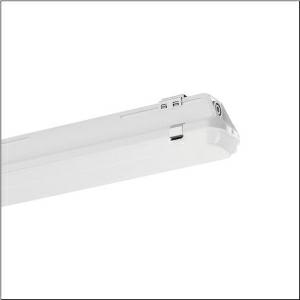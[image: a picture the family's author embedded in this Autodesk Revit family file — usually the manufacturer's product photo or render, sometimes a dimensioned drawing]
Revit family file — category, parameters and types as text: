
# Revit family: monsun_r__21_emergency_51fb20dp467c3h_1d79
name_source: partatom
category: Lighting Fixtures
units: mm (PartAtom-declared; Revit-internal decimal feet)

## family parameters
Cut with Voids When Loaded = No
Host = Face
Light Source = No
Part Type = Normal
Room Calculation Point = No
Round Connector Dimension = Use Diameter
Shared = No

## types (1)
- --- (1 x LED, 5460 lm, 36.5 W, 4000K)
    Apparent Load = 37 VA
    CIE Flux Codes = 45 75 93 94 100
    Color Rendering = 80
    Color Temperature = 4000K
    Default Elevation = 1800 mm
    Description = Monsun® 21 emergency, damp-proof luminaire, chain hanger, primary optical cover: enclosure, of PC, light emission: direct distribution, primary light characteristic: symmetric, installation type: vertical mounting, horizontal mounting, surface-mounted, suspended mounting, LED, rated luminous flux: 5.460lm, luminous efficacy: 167lm/W, light colour: 840, colour temperature: 4000K, control gear: DALI 2, with terminal, 5+3-pole, max. 2.5mm², mains connection: 220..240V, AC, 50/60Hz, rated input power: 37W, control gear: single battery element, battery: LiFePO4, 9Ah, housing, of glass-fibre reinforced polyester, uncoated, bright grey, incl. chain hanger, length: 1.590mm, width: 90mm, height: 88mm, clip for enclosure, of stainless steel (V2A), ceiling mounting element, of stainless steel (V2A), chain hanger, of stainless steel (V2A), protection rating (complete): IP66, insulation class (complete): insulation class I (protective earthing), certification: CE, UKCA, protection symbol: D, impact resistance: IK08, permissible operating ambient temperature: +5..+25°C, standard: EN 50419, EN 60598-2-1, EN 60598-2-22, corresponds to IFS (International Featured Standards) requirements for safety and quality in the food industry, for indoor or canopied outdoor use, no direct snow, no direct sun, no direct rain, LABS conformity tested according to VDMA 24364:2018-05, contact your sales advisor before using the luminaires in applications with unclear chemical exposure, large temperature fluctuations or condensation-forming humidity, packaging unit: 1 piece
    Height = 89 mm
    Lamp = 1 x LED
    Lamp Light Flux = 5460 lm
    Lamp Power = 36.5 W
    Lamp count = 1
    Length = 1590 mm
    Luminous efficacy = 150 lm/W
    Manufacturer = Siteco
    ModVariant = No
    Model = 51FB20DP467C3H
    Mounting Place = Ceiling
    Mounting Type = Surface mounted
    Number of Poles = 1
    OnlyDefault = Yes
    Power Factor = 1
    Product Name = Monsun® 21 emergency
    Product group = damp-proof luminaire
    ProductGroupID = 301
    Protection Class = Protection class I
    Protection Degree = IP 66
    RLX_Detail_Level = 1
    RLX_Emergency_Light_Flux = 0 lm
    RLX_Emergency_Type = 0
    RLX_Emergency_Type_DB = No
    RlxData = <blob elided: 92557 chars, md5=a7aa40ef>
    Socket = socket
    Standby Power = 0 W
    System Light Flux = 5460 lm
    System Power = 37 W
    Type Comments = : luminous flux: 100 % | dim-lin: 254 | 229 mA
    Type Image = l_1319656.jpg
    URL = http://relux.com
    VarID = @adj_062667
    Voltage = 0 V
    Weight = 0.00 kg
    Width = 90 mm

## geometry (parser evidence)
native form markers: Blend x4, Sweep x12
no freeform markers — native parametric forms only
